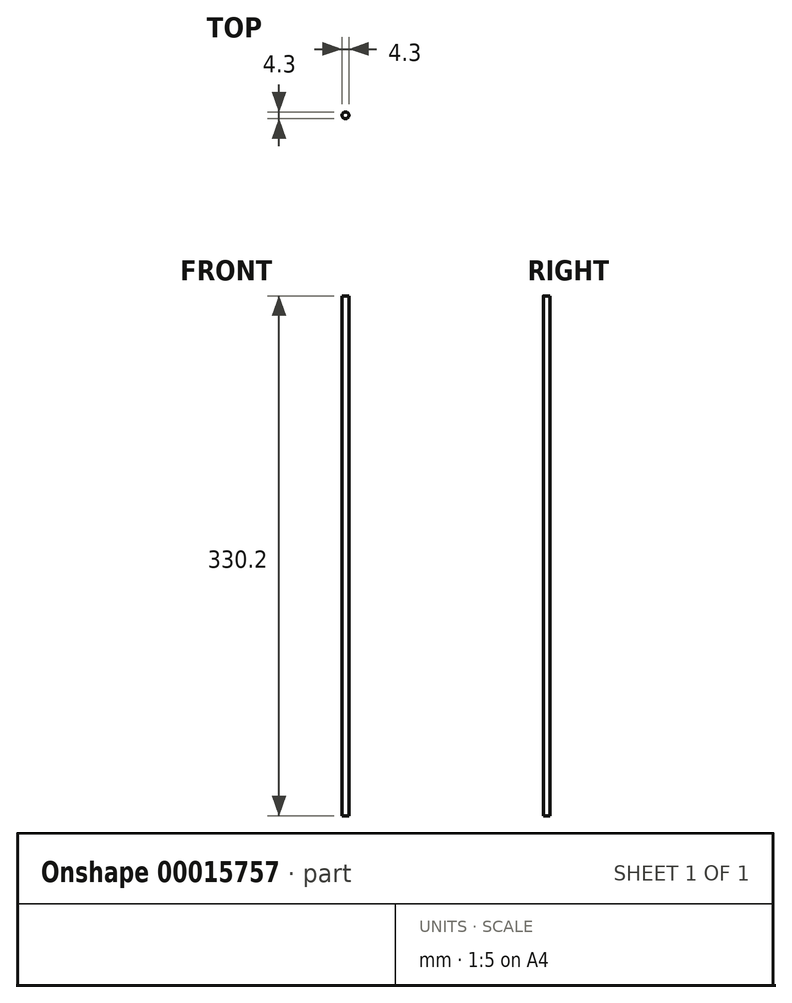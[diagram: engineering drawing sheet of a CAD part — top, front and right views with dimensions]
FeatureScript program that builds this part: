
annotation { "Feature Type Name" : "Feature", "Feature Type Description" : "" }
export const myFeature = defineFeature(function(context is Context, id is Id, definition is map)
    precondition{}
    {
        {
            var Q0;
            Q0=qCreatedBy(makeId("Top.planeOp"),FACE);
            var sketch = newSketch(context, id + "F0", { "sketchPlane" : qUnion([Q0])});
            skCircle(sketch, "E0", {"center": v(0, 0) * mm, "radius": 2.15 * mm});
            skSolve(sketch);
        }
        {
            var Q0;
            Q0=qSketchRegion(id+"F0",true);
            extrude(context, id + "F1", {"entities" : qUnion([Q0]), "depth" : 330.2 * mm});
        }
    });
